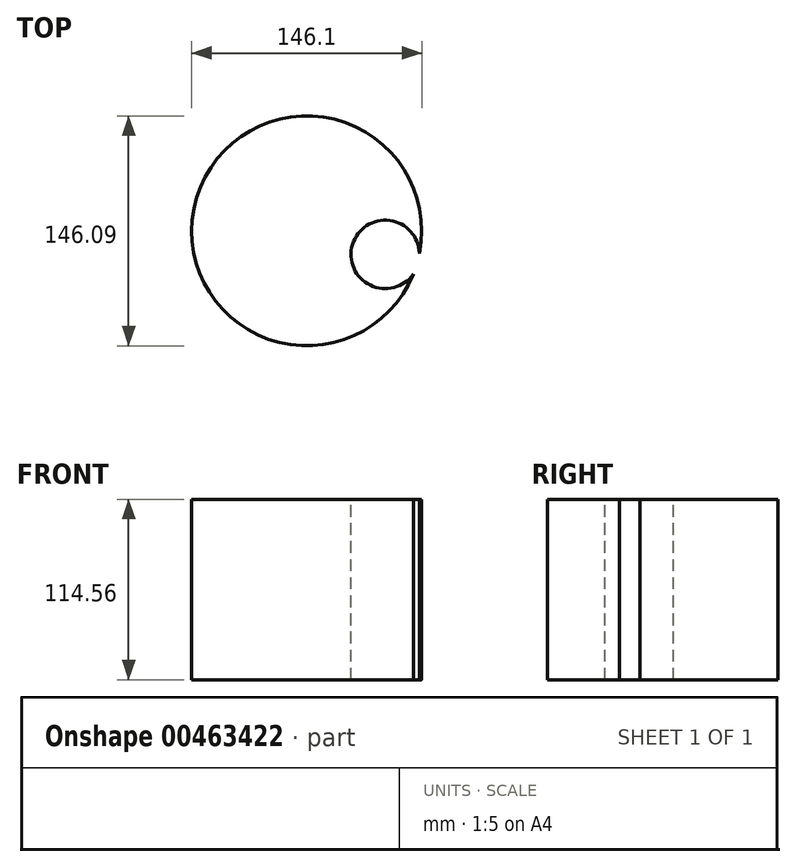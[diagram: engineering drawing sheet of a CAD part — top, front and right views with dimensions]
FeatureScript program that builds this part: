
annotation { "Feature Type Name" : "Feature", "Feature Type Description" : "" }
export const myFeature = defineFeature(function(context is Context, id is Id, definition is map)
    precondition{}
    {
        {
            var Q0;
            Q0=qCreatedBy(makeId("Top.planeOp"),FACE);
            var sketch = newSketch(context, id + "F0", { "sketchPlane" : qUnion([Q0])});
            skCircle(sketch, "E0", {"center": v(26.79, 30.8) * mm, "radius": 73.05 * mm});
            skSolve(sketch);
        }
        {
            var Q0;
            Q0 = qSketchRegion(id + "F0", true);
            extrude(context, id + "F1", {"entities" : qUnion([Q0]), "depth" : 114.56 * mm});
        }
        {
            var Q0;
            Q0=makeQuery(id+"F1.opExtrude","CAP_FACE",FACE,{"disambiguationData":[OSD([sQuery(id+"F0.wireOp",EDGE,"E0")])],"isStart":false});
            var sketch = newSketch(context, id + "F2", { "sketchPlane" : qUnion([Q0])});
            skCircle(sketch, "E1", {"center": v(76.66, 15.8) * mm, "radius": 21.75 * mm});
            skSolve(sketch);
        }
        {
            var Q0;
            {var subQ0=sQuery(id+"F2.wireOp",EDGE,"E1");var subQ1=makeQuery(id+"F1.opExtrude","CAP_EDGE",EDGE,{"disambiguationData":[OSD([sQuery(id+"F0.wireOp",EDGE,"E0")])],"isStart":false});var subQ2=makeQuery(id+"F2.imprint","INTERSECT",VERTEX,{"disambiguationData":[OD(0.0)],"derivedFrom":[subQ1,subQ0]});Q0=makeQuery(id+"F2.imprint","IMPRINT",FACE,{"disambiguationData":[TD([[makeQuery(id+"F2.imprint","IMPRINT",EDGE,{"disambiguationData":[TD([[subQ2,1.0]])],"derivedFrom":subQ0}),1.0]])]});}
            extrude(context, id + "F3", {"entities" : qUnion([Q0]), "operationType" : NewBodyOperationType.REMOVE, "oppositeDirection" : true, "depth" : 139.27 * mm});
        }
    });
